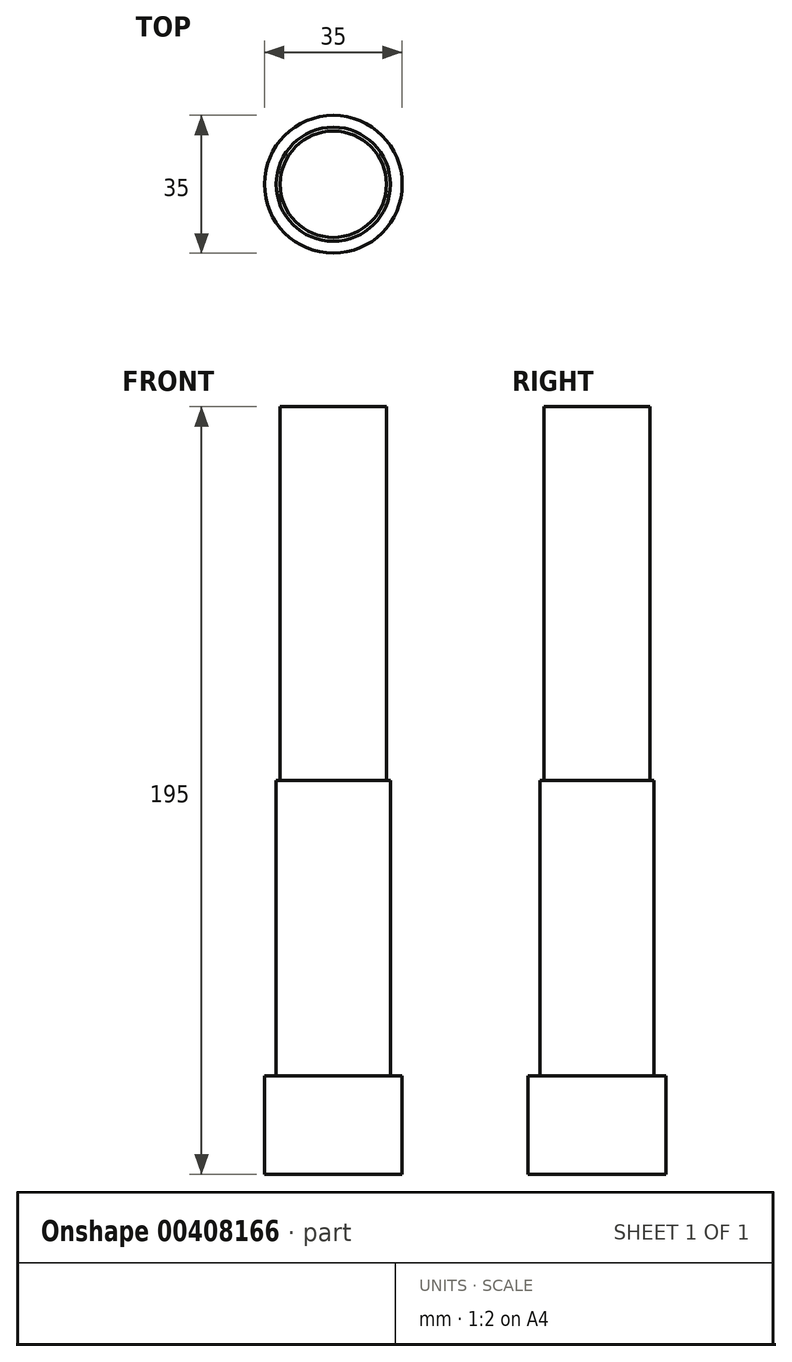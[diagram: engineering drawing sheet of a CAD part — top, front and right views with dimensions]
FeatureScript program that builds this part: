
annotation { "Feature Type Name" : "Feature", "Feature Type Description" : "" }
export const myFeature = defineFeature(function(context is Context, id is Id, definition is map)
    precondition{}
    {
        {
            var Q0;
            Q0=qCreatedBy(makeId("Top.planeOp"),FACE);
            var sketch = newSketch(context, id + "F0", { "sketchPlane" : qUnion([Q0])});
            skCircle(sketch, "E0", {"center": v(0, 0) * mm, "radius": 13.5 * mm});
            skSolve(sketch);
        }
        {
            var Q0;
            Q0=makeQuery(id+"F0.imprint","IMPRINT",FACE,{"disambiguationData":[TD([[makeQuery(id+"F0.imprint","IMPRINT",EDGE,{"derivedFrom":sQuery(id+"F0.wireOp",EDGE,"E0")}),1.0]])]});
            extrude(context, id + "F1", {"entities" : qUnion([Q0]), "depth" : 195 * mm});
        }
        {
            var Q0;
            Q0=qCreatedBy(makeId("Top.planeOp"),FACE);
            var sketch = newSketch(context, id + "F2", { "sketchPlane" : qUnion([Q0])});
            skCircle(sketch, "E1", {"center": v(0, 0) * mm, "radius": 17.5 * mm});
            skSolve(sketch);
        }
        {
            var Q0;
            Q0 = qSketchRegion(id + "F2", true);
            extrude(context, id + "F3", {"entities" : qUnion([Q0]), "operationType" : NewBodyOperationType.ADD, "depth" : 25 * mm});
        }
        {
            var Q0;
            Q0=qCreatedBy(makeId("Top.planeOp"),FACE);
            var sketch = newSketch(context, id + "F4", { "sketchPlane" : qUnion([Q0])});
            skCircle(sketch, "E2", {"center": v(0, 0) * mm, "radius": 14.5 * mm});
            skSolve(sketch);
        }
        {
            var Q0;
            Q0 = qSketchRegion(id + "F4", true);
            extrude(context, id + "F5", {"entities" : qUnion([Q0]), "operationType" : NewBodyOperationType.ADD, "depth" : 100 * mm});
        }
    });
